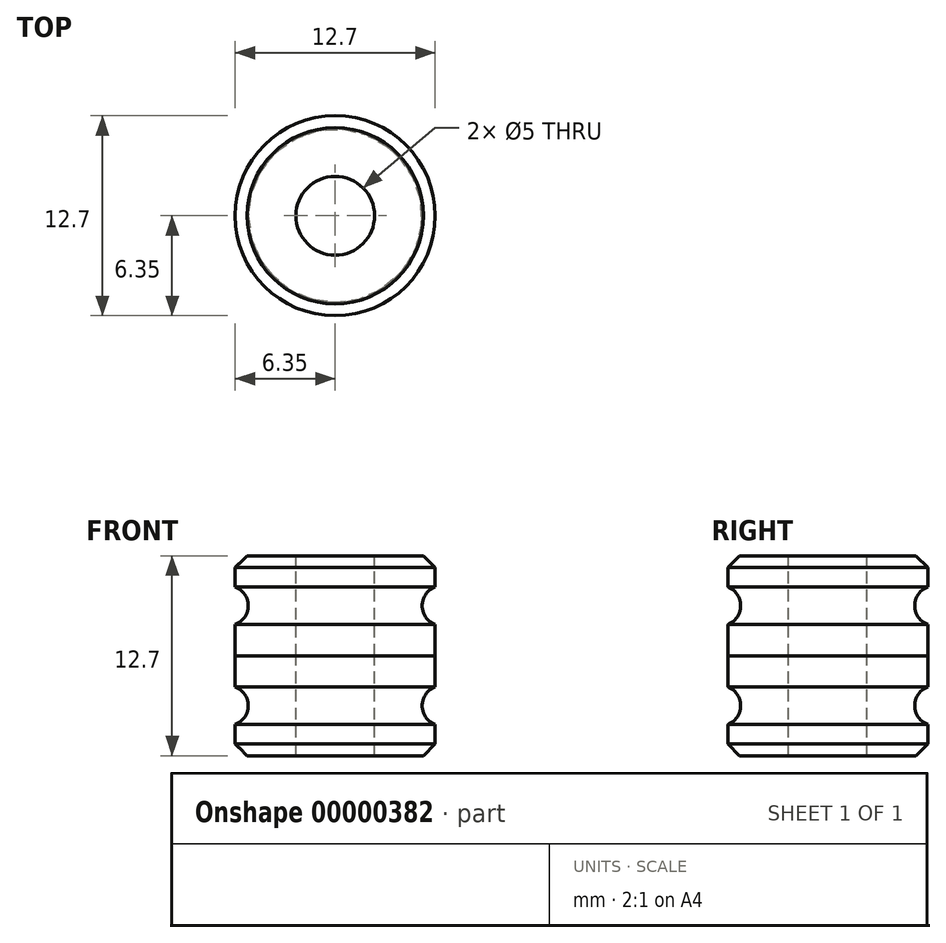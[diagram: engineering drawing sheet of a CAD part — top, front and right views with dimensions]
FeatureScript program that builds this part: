
annotation { "Feature Type Name" : "Feature", "Feature Type Description" : "" }
export const myFeature = defineFeature(function(context is Context, id is Id, definition is map)
    precondition{}
    {
        {
            var Q0;
            Q0=qCreatedBy(makeId("Front.planeOp"),FACE);
            var sketch = newSketch(context, id + "F0", { "sketchPlane" : qUnion([Q0])});
            skLineSegment(sketch, "E0", {"start": v(0, 0) * mm, "end": v(0, 10.43) * mm, "construction": true});
            skLineSegment(sketch, "E1", {"start": v(0, 0) * mm, "end": v(0, 6.35) * mm});
            skLineSegment(sketch, "E2", {"start": v(0, 6.35) * mm, "end": v(6.35, 6.35) * mm});
            skLineSegment(sketch, "E3", {"start": v(6.35, 6.35) * mm, "end": v(6.35, 0) * mm});
            skLineSegment(sketch, "E4", {"start": v(6.35, 0) * mm, "end": v(0, 0) * mm});
            skLineSegment(sketch, "E5", {"start": v(6.35, 3.17) * mm, "end": v(0, 3.17) * mm, "construction": true});
            skCircle(sketch, "E6", {"center": v(6.8, 3.18) * mm, "radius": 1.27 * mm});
            skSolve(sketch);
        }
        {
            var Q0;
            Q0=makeQuery(id+"F0.imprint","IMPRINT",FACE,{"disambiguationData":[TD([[makeQuery(id+"F0.imprint","IMPRINT",EDGE,{"derivedFrom":sQuery(id+"F0.wireOp",EDGE,"E1")}),-1.0]])]});
            var Q1;
            Q1=sQuery(id+"F0.wireOp",EDGE,"E0");
            revolve(context, id + "F1", {"entities" : qUnion([Q0]), "axis" : qUnion([Q1]), "revolveType" : RevolveType.FULL});
        }
        {
            var Q0;
            Q0=makeQuery(id+"F1.opRevolve","SWEPT_EDGE",EDGE,{"disambiguationData":[OSD([sQuery(id+"F0.wireOp",EDGE,"E2"),sQuery(id+"F0.wireOp",EDGE,"E3")])]});
            chamfer(context, id + "F2", {"entities" : qUnion([Q0]), "width" : 0.75 * mm, "tangentPropagation" : true});
        }
        {
            var Q0;
            Q0=makeQuery(id+"F1.opRevolve","SWEPT_BODY",BODY,{"disambiguationData":[OSD([sQuery(id+"F0.wireOp",EDGE,"E1"),sQuery(id+"F0.wireOp",EDGE,"E2"),sQuery(id+"F0.wireOp",EDGE,"E3"),sQuery(id+"F0.wireOp",EDGE,"E4"),sQuery(id+"F0.wireOp",EDGE,"E6")])]});
            var Q1;
            Q1=makeQuery(id+"F1.opRevolve","SWEPT_FACE",FACE,{"disambiguationData":[OSD([sQuery(id+"F0.wireOp",EDGE,"E4")])]});
            mirror(context, id + "F3", {"entities" : qUnion([Q0]), "mirrorPlane" : qUnion([Q1])});
        }
        {
            var Q0;
            Q0=makeQuery(id+"F1.opRevolve","SWEPT_FACE",FACE,{"disambiguationData":[OSD([sQuery(id+"F0.wireOp",EDGE,"E2")])]});
            var sketch = newSketch(context, id + "F4", { "sketchPlane" : qUnion([Q0])});
            skCircle(sketch, "E7", {"center": v(0, 0) * mm, "radius": 2.5 * mm});
            skSolve(sketch);
        }
        {
            var Q0;
            Q0=makeQuery(id+"F4.imprint","IMPRINT",FACE,{"disambiguationData":[TD([[makeQuery(id+"F4.imprint","IMPRINT",EDGE,{"derivedFrom":sQuery(id+"F4.wireOp",EDGE,"E7")}),1.0]])]});
            extrude(context, id + "F5", {"entities" : qUnion([Q0]), "operationType" : NewBodyOperationType.REMOVE, "endBound" : BoundingType.THROUGH_ALL, "oppositeDirection" : true, "depth" : 25 * mm});
        }
    });
